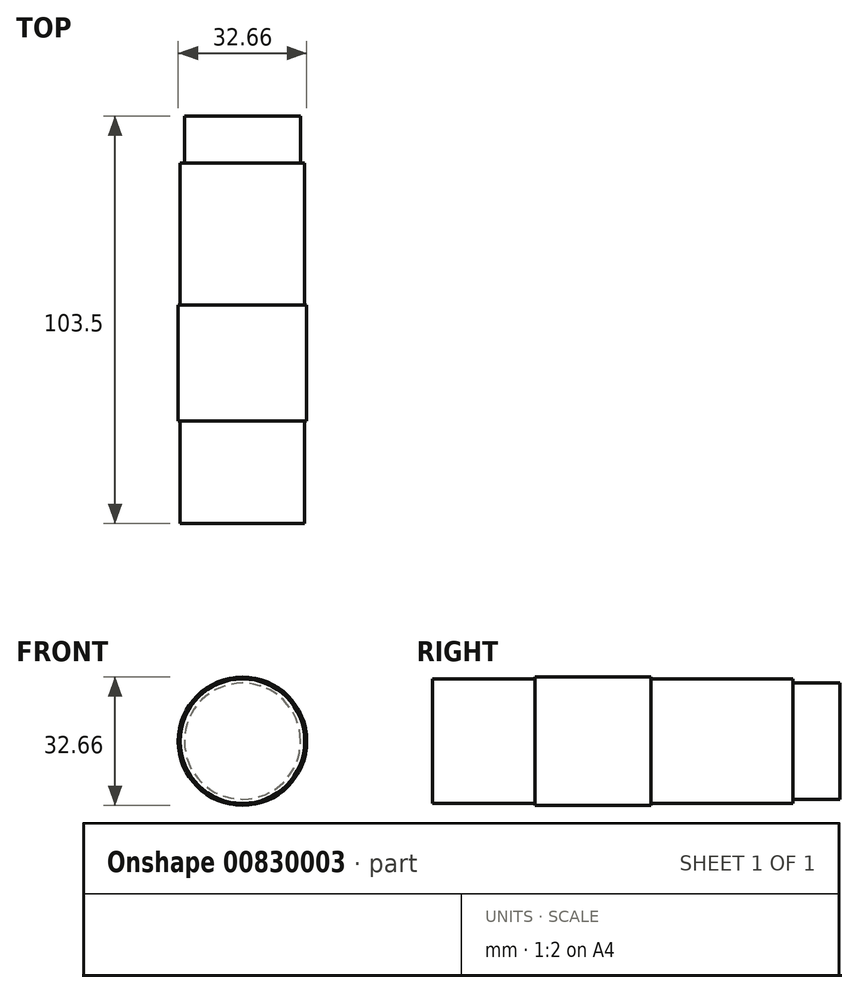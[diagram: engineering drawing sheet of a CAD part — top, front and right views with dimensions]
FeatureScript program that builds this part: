
annotation { "Feature Type Name" : "Feature", "Feature Type Description" : "" }
export const myFeature = defineFeature(function(context is Context, id is Id, definition is map)
    precondition{}
    {
        {
            var Q0;
            Q0=qCreatedBy(makeId("Top.planeOp"),FACE);
            var sketch = newSketch(context, id + "F0", { "sketchPlane" : qUnion([Q0])});
            skLineSegment(sketch, "E0", {"start": v(-15.82, 52.61) * mm, "end": v(15.82, 52.61) * mm});
            skLineSegment(sketch, "E1", {"start": v(-15.82, -38.89) * mm, "end": v(15.82, -38.89) * mm});
            skLineSegment(sketch, "E2", {"start": v(0, -65) * mm, "end": v(0, 65) * mm});
            skPoint(sketch, "E3", {"position": v(0, 52.61) * mm});
            skPoint(sketch, "E4", {"position": v(0, -38.89) * mm});
            skLineSegment(sketch, "E5", {"start": v(-16.32, 16.61) * mm, "end": v(16.32, 16.61) * mm});
            skPoint(sketch, "E6", {"position": v(0, 16.61) * mm});
            skLineSegment(sketch, "E7", {"start": v(-14.75, 64.61) * mm, "end": v(14.75, 64.61) * mm});
            skPoint(sketch, "E8", {"position": v(0, 64.61) * mm});
            skLineSegment(sketch, "E9", {"start": v(-16.32, -12.89) * mm, "end": v(16.32, -12.89) * mm});
            skPoint(sketch, "E10", {"position": v(0, -12.89) * mm});
            skLineSegment(sketch, "E11", {"start": v(-14.75, 64.61) * mm, "end": v(-14.75, 52.61) * mm});
            skLineSegment(sketch, "E12", {"start": v(-15.82, 52.61) * mm, "end": v(-15.82, 16.61) * mm});
            skLineSegment(sketch, "E13", {"start": v(-16.32, -12.89) * mm, "end": v(-16.32, 16.61) * mm});
            skLineSegment(sketch, "E14", {"start": v(-15.82, -38.89) * mm, "end": v(-15.82, -12.89) * mm});
            skLineSegment(sketch, "E15.MirrorCS", {"start": v(14.75, 64.61) * mm, "end": v(14.75, 52.61) * mm});
            skLineSegment(sketch, "E16.MirrorCS", {"start": v(15.82, -38.89) * mm, "end": v(15.82, -12.89) * mm});
            skLineSegment(sketch, "E17.MirrorCS", {"start": v(16.32, -12.89) * mm, "end": v(16.32, 16.61) * mm});
            skLineSegment(sketch, "E18.MirrorCS", {"start": v(15.82, 52.61) * mm, "end": v(15.82, 16.61) * mm});
            skSolve(sketch);
        }
        {
            var Q0;
            {var subQ0=sQuery(id+"F0.wireOp",EDGE,"E11");Q0=makeQuery(id+"F0.imprint","IMPRINT",FACE,{"disambiguationData":[TD([[makeQuery(id+"F0.imprint","IMPRINT",EDGE,{"derivedFrom":subQ0}),1.0]])]});}
            var Q1;
            {var subQ5=sQuery(id+"F0.wireOp",EDGE,"E12");Q1=makeQuery(id+"F0.imprint","IMPRINT",FACE,{"disambiguationData":[TD([[makeQuery(id+"F0.imprint","IMPRINT",EDGE,{"derivedFrom":subQ5}),1.0]])]});}
            var Q2;
            {var subQ0=sQuery(id+"F0.wireOp",EDGE,"E13");Q2=makeQuery(id+"F0.imprint","IMPRINT",FACE,{"disambiguationData":[TD([[makeQuery(id+"F0.imprint","IMPRINT",EDGE,{"derivedFrom":subQ0}),-1.0]])]});}
            var Q3;
            {var subQ0=sQuery(id+"F0.wireOp",EDGE,"E14");Q3=makeQuery(id+"F0.imprint","IMPRINT",FACE,{"disambiguationData":[TD([[makeQuery(id+"F0.imprint","IMPRINT",EDGE,{"derivedFrom":subQ0}),-1.0]])]});}
            var Q4;
            Q4=sQuery(id+"F0.wireOp",EDGE,"E2");
            revolve(context, id + "F1", {"surfaceOperationType" : NewSurfaceOperationType.NEW, "entities" : qUnion([Q0, Q1, Q2, Q3]), "axis" : qUnion([Q4]), "revolveType" : RevolveType.FULL});
        }
    });
